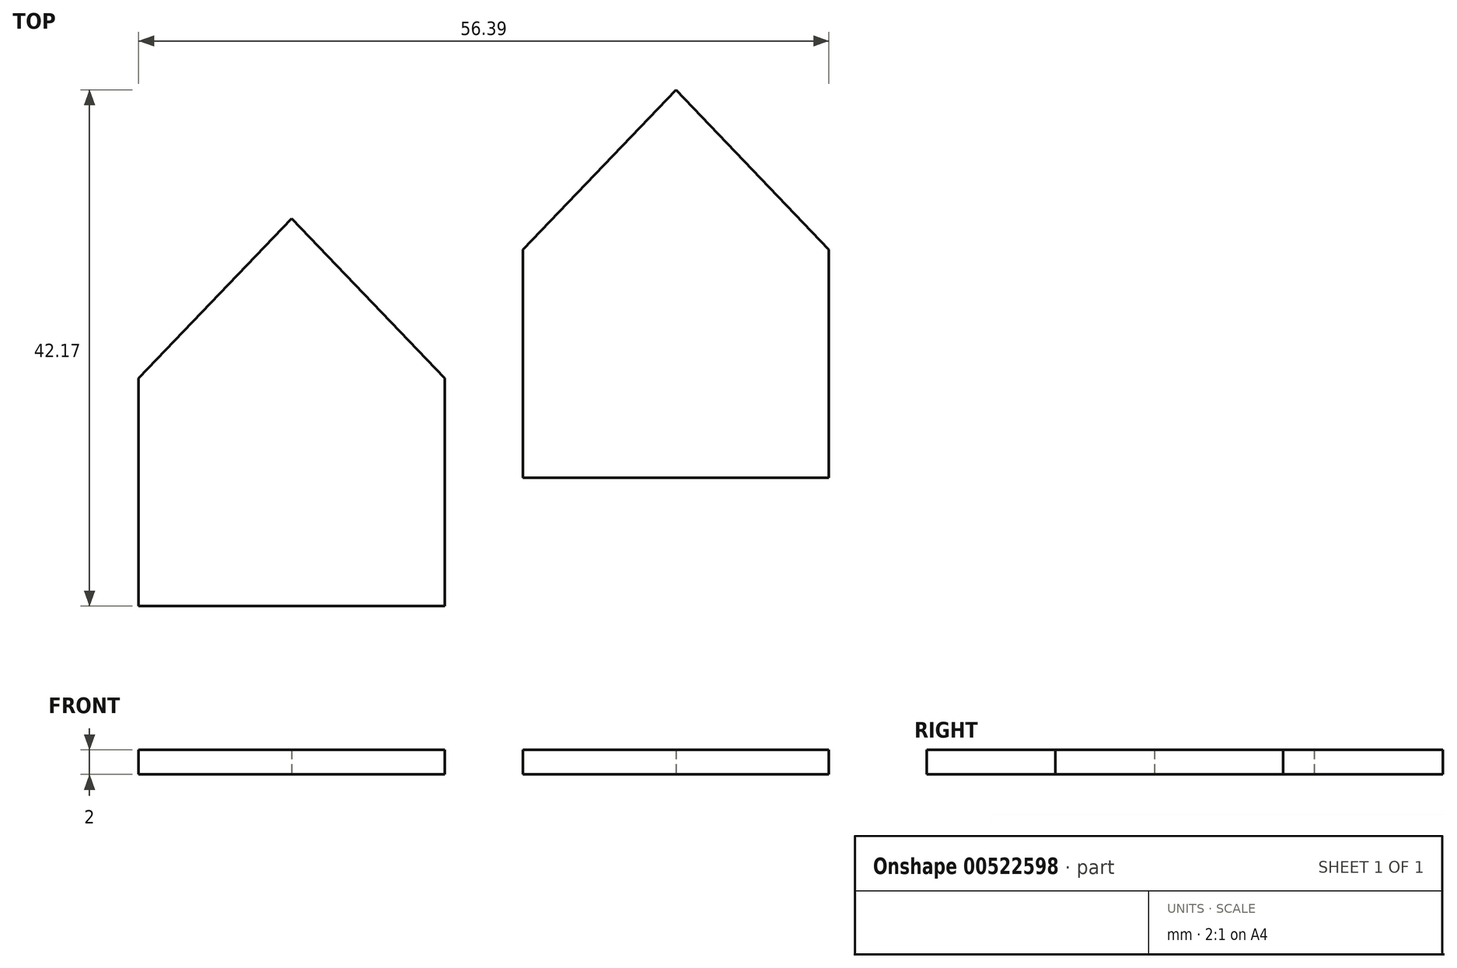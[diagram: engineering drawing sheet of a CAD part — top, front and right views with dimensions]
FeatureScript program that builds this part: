
annotation { "Feature Type Name" : "Feature", "Feature Type Description" : "" }
export const myFeature = defineFeature(function(context is Context, id is Id, definition is map)
    precondition{}
    {
        {
            var Q0;
            Q0=qCreatedBy(makeId("Top.planeOp"),FACE);
            var sketch = newSketch(context, id + "F0", { "sketchPlane" : qUnion([Q0])});
            skLineSegment(sketch, "E0", {"start": v(-31.39, 8.1) * mm, "end": v(-31.39, -10.5) * mm});
            skLineSegment(sketch, "E1", {"start": v(-31.39, -10.5) * mm, "end": v(-6.39, -10.5) * mm});
            skLineSegment(sketch, "E2", {"start": v(-6.39, -10.5) * mm, "end": v(-6.39, 8.1) * mm});
            skLineSegment(sketch, "E3", {"start": v(-6.39, 8.1) * mm, "end": v(-18.89, 21.16) * mm});
            skLineSegment(sketch, "E4", {"start": v(-18.89, 21.16) * mm, "end": v(-31.39, 8.1) * mm});
            skPoint(sketch, "E5", {"position": v(-18.89, -10.5) * mm});
            skSolve(sketch);
        }
        {
            var Q0;
            Q0=makeQuery(id+"F0.imprint","IMPRINT",FACE,{"disambiguationData":[TD([[makeQuery(id+"F0.imprint","IMPRINT",EDGE,{"derivedFrom":sQuery(id+"F0.wireOp",EDGE,"E0")}),1.0]])]});
            extrude(context, id + "F1", {"entities" : qUnion([Q0]), "depth" : 2 * mm, "offsetDistance" : 25 * mm});
        }
        {
            var Q0;
            Q0=qCreatedBy(makeId("Top.planeOp"),FACE);
            var sketch = newSketch(context, id + "F2", { "sketchPlane" : qUnion([Q0])});
            skLineSegment(sketch, "E6", {"start": v(0, 0) * mm, "end": v(0, 18.61) * mm});
            skLineSegment(sketch, "E7", {"start": v(0, 18.61) * mm, "end": v(12.5, 31.67) * mm});
            skLineSegment(sketch, "E8", {"start": v(0, 0) * mm, "end": v(25, 0) * mm});
            skLineSegment(sketch, "E9", {"start": v(25, 0) * mm, "end": v(25, 18.61) * mm});
            skLineSegment(sketch, "E10", {"start": v(25, 18.61) * mm, "end": v(12.5, 31.67) * mm});
            skSolve(sketch);
        }
        {
            var Q0;
            Q0 = qSketchRegion(id + "F2", true);
            extrude(context, id + "F3", {"entities" : qUnion([Q0]), "depth" : 2 * mm, "offsetDistance" : 25 * mm});
        }
    });
